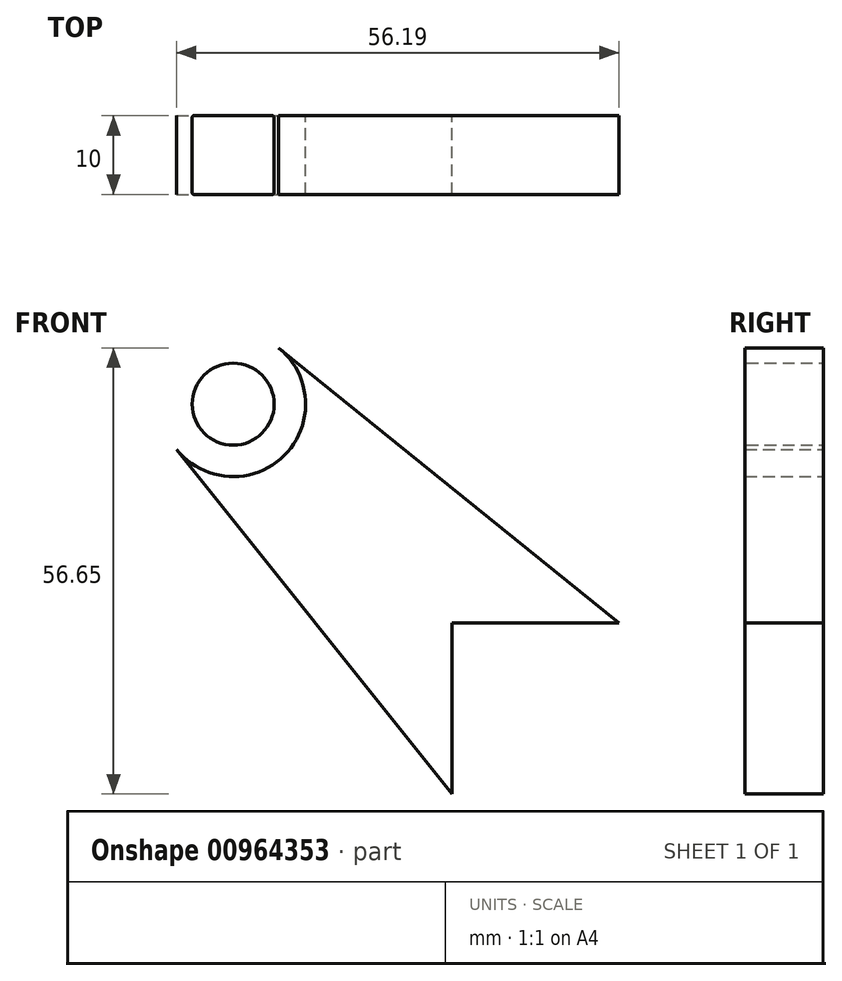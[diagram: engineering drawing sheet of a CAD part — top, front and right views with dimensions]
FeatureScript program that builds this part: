
annotation { "Feature Type Name" : "Feature", "Feature Type Description" : "" }
export const myFeature = defineFeature(function(context is Context, id is Id, definition is map)
    precondition{}
    {
        {
            var Q0;
            Q0=qCreatedBy(makeId("Front.planeOp"),FACE);
            var sketch = newSketch(context, id + "F0", { "sketchPlane" : qUnion([Q0])});
            skLineSegment(sketch, "E0.bottom", {"start": v(10.1, -10.1) * mm, "end": v(-10.1, -10.1) * mm, "construction": true});
            skLineSegment(sketch, "E0.top", {"start": v(10.1, 10.1) * mm, "end": v(-10.1, 10.1) * mm});
            skLineSegment(sketch, "E0.left", {"start": v(10.1, -10.1) * mm, "end": v(10.1, 10.1) * mm, "construction": true});
            skLineSegment(sketch, "E0.right", {"start": v(-10.1, -10.1) * mm, "end": v(-10.1, 10.1) * mm, "construction": true});
            skPoint(sketch, "E0.middle", {"position": v(0, 0) * mm});
            skCircle(sketch, "E1", {"center": v(0, 0) * mm, "radius": 2.9 * mm, "construction": true});
            skLineSegment(sketch, "E2", {"start": v(-2.9, 10.1) * mm, "end": v(-2.9, -10.1) * mm, "construction": true});
            skLineSegment(sketch, "E3", {"start": v(2.9, 10.1) * mm, "end": v(2.9, -10.1) * mm, "construction": true});
            skLineSegment(sketch, "E4", {"start": v(-10.1, 2.9) * mm, "end": v(10.1, 2.9) * mm, "construction": true});
            skLineSegment(sketch, "E5", {"start": v(-10.1, -2.9) * mm, "end": v(10.1, -2.9) * mm, "construction": true});
            skLineSegment(sketch, "E6", {"start": v(-10.1, 10.1) * mm, "end": v(-2.9, 10.1) * mm});
            skLineSegment(sketch, "E7", {"start": v(-2.9, 10.1) * mm, "end": v(-2.9, 8.1) * mm});
            skLineSegment(sketch, "E8", {"start": v(-2.9, 8.1) * mm, "end": v(2.9, 8.1) * mm});
            skLineSegment(sketch, "E9", {"start": v(2.9, 8.1) * mm, "end": v(2.9, 10.1) * mm});
            skLineSegment(sketch, "E10", {"start": v(2.9, 10.1) * mm, "end": v(9.1, 10.1) * mm});
            skLineSegment(sketch, "E11", {"start": v(9.1, 10.1) * mm, "end": v(9.1, 12.1) * mm});
            skLineSegment(sketch, "E12", {"start": v(9.1, 12.1) * mm, "end": v(-12.1, 12.1) * mm});
            skLineSegment(sketch, "E13", {"start": v(-12.1, 12.1) * mm, "end": v(-12.1, -9.6) * mm});
            skLineSegment(sketch, "E14", {"start": v(-12.1, -9.6) * mm, "end": v(-10.1, -9.6) * mm});
            skLineSegment(sketch, "E15", {"start": v(-10.1, -9.6) * mm, "end": v(-10.1, -2.9) * mm});
            skLineSegment(sketch, "E16", {"start": v(-10.1, -2.9) * mm, "end": v(-8.1, -2.9) * mm});
            skLineSegment(sketch, "E17", {"start": v(-8.1, -2.9) * mm, "end": v(-8.1, 2.9) * mm});
            skLineSegment(sketch, "E18", {"start": v(-8.1, 2.9) * mm, "end": v(-10.1, 2.9) * mm});
            skLineSegment(sketch, "E19", {"start": v(-10.1, 2.9) * mm, "end": v(-10.1, 10.1) * mm});
            skCircle(sketch, "E20", {"center": v(0, 0) * mm, "radius": 8.1 * mm, "construction": true});
            skLineSegment(sketch, "E21", {"start": v(0, 0) * mm, "end": v(-12.1, 12.1) * mm, "construction": true});
            skCircle(sketch, "E22", {"center": v(-39.9, 39.9) * mm, "radius": 5.2 * mm});
            skCircle(sketch, "E23", {"center": v(-39.9, 39.9) * mm, "radius": 9.2 * mm});
            skLineSegment(sketch, "E24", {"start": v(-34.11, 47.05) * mm, "end": v(9.1, 12.1) * mm});
            skLineSegment(sketch, "E25", {"start": v(-47.09, 34.15) * mm, "end": v(-12.1, -9.6) * mm});
            skSolve(sketch);
        }
        {
            var Q0;
            {var subQ0=sQuery(id+"F0.wireOp",EDGE,"E6");Q0=makeQuery(id+"F0.imprint","IMPRINT",FACE,{"disambiguationData":[TD([[makeQuery(id+"F0.imprint","IMPRINT",EDGE,{"derivedFrom":subQ0}),1.0]])]});}
            var Q1;
            Q1=makeQuery(id+"F0.imprint","IMPRINT",FACE,{"disambiguationData":[TD([[makeQuery(id+"F0.imprint","IMPRINT",EDGE,{"derivedFrom":sQuery(id+"F0.wireOp",EDGE,"E12")}),-1.0]])]});
            var Q2;
            Q2=makeQuery(id+"F0.imprint","IMPRINT",FACE,{"disambiguationData":[TD([[makeQuery(id+"F0.imprint","IMPRINT",EDGE,{"derivedFrom":sQuery(id+"F0.wireOp",EDGE,"E22")}),1.0]])]});
            extrude(context, id + "F1", {"entities" : qUnion([Q0, Q1, Q2]), "depth" : 10 * mm, "offsetDistance" : 25 * mm});
        }
        {
            var Q0;
            Q0=makeQuery(id+"F1.opExtrude","SWEPT_FACE",FACE,{"disambiguationData":[OSD([sQuery(id+"F0.wireOp",EDGE,"E17")])]});
            var Q1;
            Q1=makeQuery(id+"F1.opExtrude","SWEPT_FACE",FACE,{"disambiguationData":[OSD([sQuery(id+"F0.wireOp",EDGE,"E19")])]});
            var Q2;
            Q2=makeQuery(id+"F1.opExtrude","SWEPT_FACE",FACE,{"disambiguationData":[OSD([sQuery(id+"F0.wireOp",EDGE,"E15")])]});
            var Q3;
            Q3=makeQuery(id+"F1.opExtrude","SWEPT_FACE",FACE,{"disambiguationData":[OSD([sQuery(id+"F0.wireOp",EDGE,"E10")])]});
            var Q4;
            Q4=makeQuery(id+"F1.opExtrude","SWEPT_FACE",FACE,{"disambiguationData":[OSD([sQuery(id+"F0.wireOp",EDGE,"E8")])]});
            var Q5;
            Q5=makeQuery(id+"F1.opExtrude","SWEPT_FACE",FACE,{"disambiguationData":[OSD([sQuery(id+"F0.wireOp",EDGE,"E6")])]});
            var Q6;
            Q6=makeQuery(id+"F1.opExtrude","CAP_FACE",FACE,{"disambiguationData":[OSD([sQuery(id+"F0.wireOp",EDGE,"E6"),sQuery(id+"F0.wireOp",EDGE,"E7"),sQuery(id+"F0.wireOp",EDGE,"E8"),sQuery(id+"F0.wireOp",EDGE,"E9"),sQuery(id+"F0.wireOp",EDGE,"E10"),sQuery(id+"F0.wireOp",EDGE,"E11"),sQuery(id+"F0.wireOp",EDGE,"E14"),sQuery(id+"F0.wireOp",EDGE,"E15"),sQuery(id+"F0.wireOp",EDGE,"E16"),sQuery(id+"F0.wireOp",EDGE,"E17"),sQuery(id+"F0.wireOp",EDGE,"E18"),sQuery(id+"F0.wireOp",EDGE,"E19"),sQuery(id+"F0.wireOp",EDGE,"E22"),sQuery(id+"F0.wireOp",EDGE,"E23"),sQuery(id+"F0.wireOp",EDGE,"E24"),sQuery(id+"F0.wireOp",EDGE,"E25")])],"isStart":true});
            var Q7;
            Q7=makeQuery(id+"F1.opExtrude","CAP_FACE",FACE,{"disambiguationData":[OSD([sQuery(id+"F0.wireOp",EDGE,"E6"),sQuery(id+"F0.wireOp",EDGE,"E7"),sQuery(id+"F0.wireOp",EDGE,"E8"),sQuery(id+"F0.wireOp",EDGE,"E9"),sQuery(id+"F0.wireOp",EDGE,"E10"),sQuery(id+"F0.wireOp",EDGE,"E11"),sQuery(id+"F0.wireOp",EDGE,"E14"),sQuery(id+"F0.wireOp",EDGE,"E15"),sQuery(id+"F0.wireOp",EDGE,"E16"),sQuery(id+"F0.wireOp",EDGE,"E17"),sQuery(id+"F0.wireOp",EDGE,"E18"),sQuery(id+"F0.wireOp",EDGE,"E19"),sQuery(id+"F0.wireOp",EDGE,"E22"),sQuery(id+"F0.wireOp",EDGE,"E23"),sQuery(id+"F0.wireOp",EDGE,"E24"),sQuery(id+"F0.wireOp",EDGE,"E25")])],"isStart":false});
            fillet(context, id + "F2", {"entities" : qUnion([Q0, Q1, Q2, Q3, Q4, Q5, Q6, Q7]), "tangentPropagation" : true, "radius" : .2 * mm, "defaultsChanged" : false, "vertexSettings" : [], "allowEdgeOverflow" : false});
        }
    });
